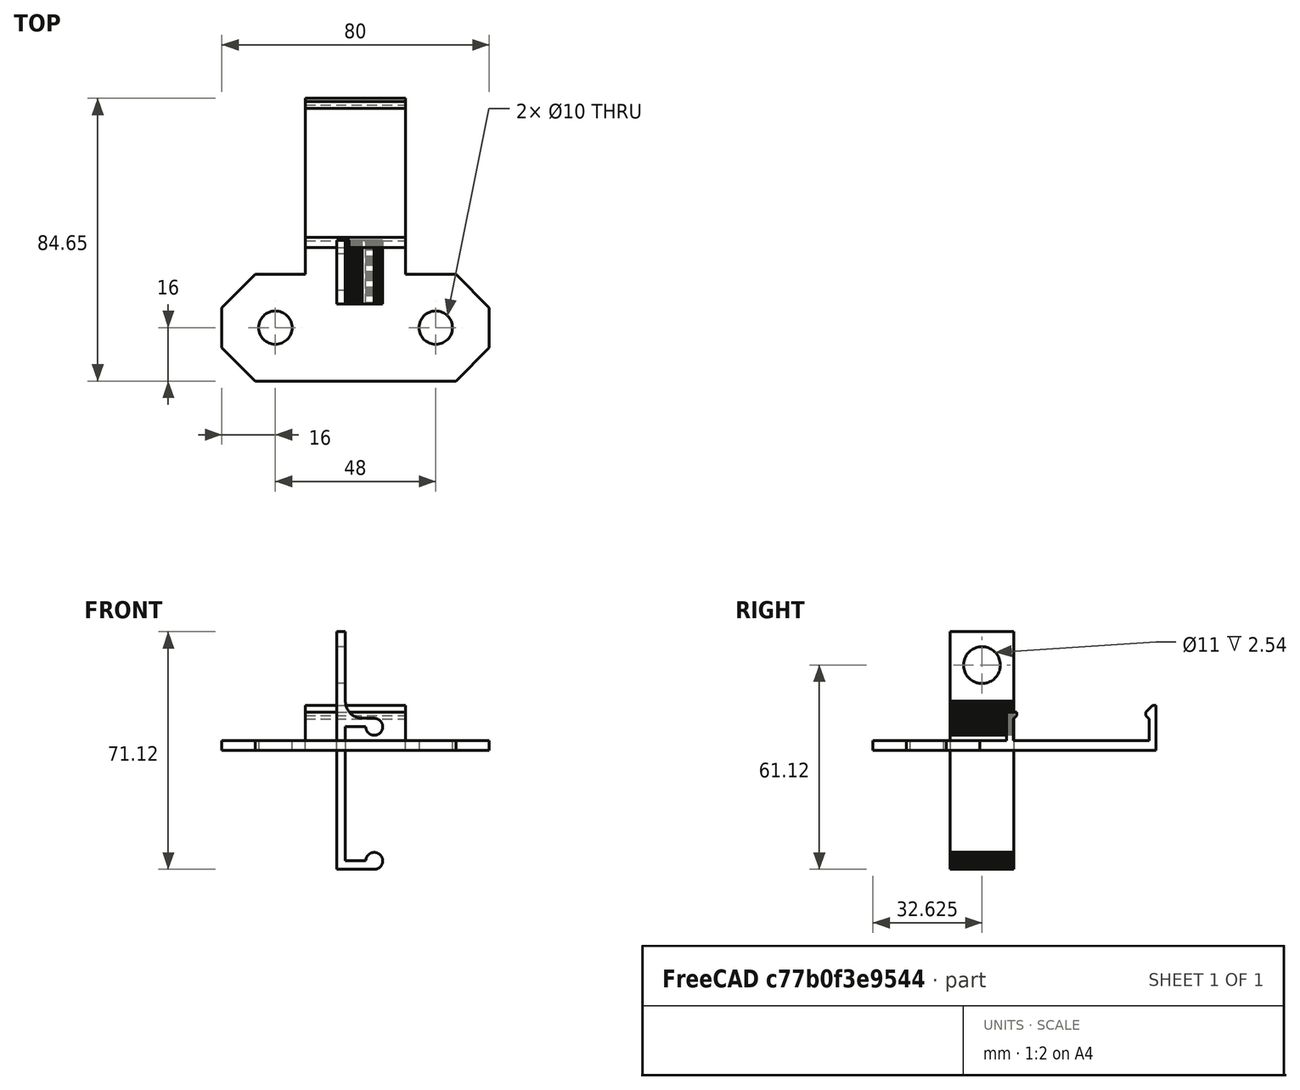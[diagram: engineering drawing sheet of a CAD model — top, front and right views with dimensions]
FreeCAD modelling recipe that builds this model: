
FCSTD DOCUMENT  (FreeCAD 0.20RUnknown)
Label: FilamentGuideRemix
License: All rights reserved
LicenseURL: http://en.wikipedia.org/wiki/All_rights_reserved
objects: Sketcher::SketchObject×7, PartDesign::Pocket×3, PartDesign::Pad×3, Part::Feature×2, PartDesign::Body×2, Mesh::Feature×1, PartDesign::FeatureBase×1, PartDesign::Plane×1, PartDesign::Hole×1, PartDesign::Chamfer×1
note: 29 computed .brp shape members not serialized (recipe doc carries the construction recipe); baked Part::Feature solids carry a one-line shape summary decoded from their .brp

FEATURE [Mesh::Feature] filament_guide2_clamp2  label="filament-guide2-clamp2"
FEATURE [Part::Feature] filament_guide2_clamp2001
  shape: bbox 21.34 x 19.05 x 71.12 mm, 2724 faces, 0 solids (baked)
FEATURE [Part::Feature] filament_guide2_clamp2001_solid  label="filament_guide2_clamp2001 (Solid)"
  shape: bbox 21.34 x 19.05 x 71.12 mm, 2724 faces (baked)
FEATURE [PartDesign::FeatureBase] BaseFeature
  BaseFeature = -> filament_guide2_clamp2001_solid
FEATURE [PartDesign::Plane] DatumPlane
  Length = 60
  MapMode = 5
  Placement = pos=(0,0,35.56) rot=(0,0,1;0rad)
  ResizeMode = 0
  Support = -> [BaseFeature]
  Width = 60
FEATURE [Sketcher::SketchObject] Sketch
  FullyConstrained = false
  MapMode = 5
  Placement = pos=(0,0,35.56) rot=(0,0,1;0rad)
  Support = -> [DatumPlane]
  sketch-geometry (4):
    g0: LineSegment StartX=-15.8199 StartY=4.12834 StartZ=0 EndX=12.2154 EndY=4.12834 EndZ=0
    g1: LineSegment StartX=12.2154 StartY=4.12834 StartZ=0 EndX=12.2154 EndY=-23.4291 EndZ=0
    g2: LineSegment StartX=12.2154 StartY=-23.4291 StartZ=0 EndX=-15.8199 EndY=-23.4291 EndZ=0
    g3: LineSegment StartX=-15.8199 StartY=-23.4291 StartZ=0 EndX=-15.8199 EndY=4.12834 EndZ=0
  constraints (8):
    c: Coincident(g0,g1)
    c: Coincident(g1,g2)
    c: Coincident(g2,g3)
    c: Coincident(g3,g0)
    c: Horizontal(g0)
    c: Horizontal(g2)
    c: Vertical(g1)
    c: Vertical(g3)
FEATURE [PartDesign::Pocket] Pocket
  BaseFeature = -> BaseFeature
  Direction = (0,0,-1)
  Length = 15
  Length2 = 5
  Profile = -> Sketch
  ReferenceAxis = -> Sketch [N_Axis]
  Type = 0
FEATURE [Sketcher::SketchObject] Sketch001
  ExternalGeometry = -> [Pocket]
  FullyConstrained = true
  MapMode = 5
  Placement = pos=(0,0,20.56) rot=(0,0,1;0rad)
  Support = -> [Pocket]
  sketch-geometry (4):
    g0: LineSegment StartX=-5.588 StartY=0 StartZ=0 EndX=-3.048 EndY=0 EndZ=0
    g1: LineSegment StartX=-3.048 StartY=0 StartZ=0 EndX=-3.048 EndY=-19.05 EndZ=0
    g2: LineSegment StartX=-3.048 StartY=-19.05 StartZ=0 EndX=-5.588 EndY=-19.05 EndZ=0
    g3: LineSegment StartX=-5.588 StartY=-19.05 StartZ=0 EndX=-5.588 EndY=0 EndZ=0
  constraints (10):
    c: Coincident(g0,g1)
    c: Coincident(g1,g2)
    c: Coincident(g2,g3)
    c: Coincident(g3,g0)
    c: Horizontal(g0)
    c: Horizontal(g2)
    c: Vertical(g1)
    c: Vertical(g3)
    c: Coincident(g0,g-3)
    c: Coincident(g1,g-6)
FEATURE [PartDesign::Pad] Pad
  BaseFeature = -> Pocket
  Direction = (0,0,1)
  Length = 15
  Length2 = 10
  Profile = -> Sketch001
  ReferenceAxis = -> Sketch001 [N_Axis]
  Type = 0
FEATURE [Sketcher::SketchObject] Sketch002
  ExternalGeometry = -> [Pad]
  FullyConstrained = true
  MapMode = 5
  Placement = pos=(-3.048,0,0) rot=(0.57735,0.57735,0.57735;2.0944rad)
  Support = -> [Pad]
  sketch-geometry (4):
    g0: Circle CenterX=-9.525 CenterY=25.56 CenterZ=0 NormalX=0 NormalY=0 NormalZ=1 AngleXU=0 Radius=2.5
    g1: LineSegment StartX=-19.05 StartY=35.56 StartZ=0 EndX=-9.525 EndY=35.56 EndZ=0
    g2: LineSegment StartX=0 StartY=35.56 StartZ=0 EndX=-9.525 EndY=35.56 EndZ=0
    g3: LineSegment StartX=-9.525 StartY=35.56 StartZ=0 EndX=-9.525 EndY=25.56 EndZ=0
  constraints (10):
    c: Diameter(g0) = 5
    c: Coincident(g1,g-5)
    c: PointOnObject(g1,g-3)
    c: Coincident(g2,g-3)
    c: Coincident(g2,g1)
    c: Equal(g1,g2)
    c: Coincident(g3,g1)
    c: Coincident(g3,g0)
    c: Vertical(g3)
    c: DistanceY(g3,g3) = 10
FEATURE [PartDesign::Hole] Hole
  BaseFeature = -> Pad
  CustomThreadClearance = 0
  Depth = 25
  DepthType = 0
  Diameter = 11
  DrillForDepth = false
  DrillPoint = 1
  DrillPointAngle = 118
  HoleCutCountersinkAngle = 90
  HoleCutCustomValues = false
  HoleCutDepth = 0
  HoleCutDiameter = 6.1
  HoleCutType = 0
  ModelThread = false
  Profile = -> Sketch002
  Tapered = false
  TaperedAngle = 90
  ThreadClass = 0
  ThreadDepth = 25
  ThreadDepthType = 0
  ThreadDirection = 0
  ThreadFit = 0
  ThreadSize = 18
  ThreadType = 1
  Threaded = false
  UseCustomThreadClearance = false
FEATURE [PartDesign::Body] Body
  BaseFeature = -> filament_guide2_clamp2001_solid
  Group = -> [BaseFeature,DatumPlane,Sketch,Pocket,Sketch001,Pad,Sketch002,Hole]
  Origin = -> Origin
  Tip = -> Hole
FEATURE [Sketcher::SketchObject] Sketch003
  FullyConstrained = true
  MapMode = 5
  Placement = pos=(0,0,0) rot=(0.57735,0.57735,0.57735;2.0944rad)
  Support = -> [YZ_Plane001]
  expr: Constraints[48] = 90 + 45
  expr: Constraints[49] = 90 + 45
  sketch-geometry (19):
    g0: LineSegment StartX=0 StartY=3.15 StartZ=0 EndX=40.35 EndY=3.15 EndZ=0
    g1: LineSegment StartX=40.35 StartY=3.15 StartZ=0 EndX=40.35 EndY=9.35 EndZ=0
    g2: LineSegment StartX=40.35 StartY=9.35 StartZ=0 EndX=0 EndY=9.35 EndZ=0
    g3: LineSegment StartX=0 StartY=9.35 StartZ=0 EndX=0 EndY=3.15 EndZ=0
    g4: LineSegment StartX=42.5 StartY=0 StartZ=0 EndX=42.5 EndY=11.5 EndZ=0
    g5: LineSegment StartX=42.5 StartY=11.5 StartZ=0 EndX=39.5 EndY=11.5 EndZ=0
    g6: LineSegment StartX=39.5 StartY=11.5 StartZ=0 EndX=39.5 EndY=10.5 EndZ=0
    g7: LineSegment StartX=39.5 StartY=10.5 StartZ=0 EndX=40.5 EndY=9.5 EndZ=0
    g8: LineSegment StartX=40.5 StartY=9.5 StartZ=0 EndX=40.5 EndY=3 EndZ=0
    g9: LineSegment StartX=40.5 StartY=3 StartZ=0 EndX=-0.15 EndY=3 EndZ=0
    g10: LineSegment StartX=-0.15 StartY=3 StartZ=0 EndX=-0.15 EndY=9.5 EndZ=0
    g11: LineSegment StartX=-0.15 StartY=9.5 StartZ=0 EndX=0.85 EndY=10.5 EndZ=0
    g12: LineSegment StartX=0.85 StartY=10.5 StartZ=0 EndX=0.85 EndY=11.5 EndZ=0
    g13: LineSegment StartX=0.85 StartY=11.5 StartZ=0 EndX=-2.15 EndY=11.5 EndZ=0
    g14: LineSegment StartX=-2.15 StartY=11.5 StartZ=0 EndX=-2.15 EndY=3 EndZ=0
    g15: LineSegment StartX=-2.15 StartY=3 StartZ=0 EndX=-42.15 EndY=3 EndZ=0
    g16: LineSegment StartX=-42.15 StartY=3 StartZ=0 EndX=-42.15 EndY=0 EndZ=0
    g17: LineSegment StartX=-42.15 StartY=0 StartZ=0 EndX=42.5 EndY=0 EndZ=0
    g18: LineSegment StartX=-2.15 StartY=3 StartZ=0 EndX=-0.15 EndY=3 EndZ=0
  constraints (56):
    c: Coincident(g0,g1)
    c: Coincident(g1,g2)
    c: Coincident(g2,g3)
    c: Coincident(g3,g0)
    c: Horizontal(g0)
    c: Horizontal(g2)
    c: Vertical(g1)
    c: Vertical(g3)
    c: DistanceX(g2,g2) = 40.35
    c: DistanceY(g1,g1) = 6.2
    c: PointOnObject(g0,g-2)
    c: PointOnObject(g4,g-1)
    c: Vertical(g4)
    c: Coincident(g4,g5)
    c: Horizontal(g5)
    c: Coincident(g5,g6)
    c: Vertical(g6)
    c: Coincident(g6,g7)
    c: Coincident(g7,g8)
    c: Coincident(g8,g9)
    c: Horizontal(g9)
    c: Coincident(g9,g10)
    c: Vertical(g10)
    c: Coincident(g10,g11)
    c: Coincident(g11,g12)
    c: Vertical(g12)
    c: Coincident(g12,g13)
    c: Horizontal(g13)
    c: Coincident(g13,g14)
    c: Vertical(g14)
    c: Coincident(g14,g15)
    c: Horizontal(g15)
    c: Coincident(g15,g16)
    c: PointOnObject(g16,g-1)
    c: Vertical(g16)
    c: Coincident(g16,g17)
    c: Coincident(g17,g4)
    c: Vertical(g8)
    c: Coincident(g18,g14)
    c: Coincident(g18,g9)
    c: Horizontal(g18)
    c: DistanceY(g9,g0) = 0.15
    c: DistanceX(g0,g8) = 0.15
    c: DistanceX(g9,g0) = 0.15
    c: DistanceY(g2,g10) = 0.15
    c: Equal(g8,g10)
    c: Equal(g12,g6)
    c: Equal(g11,g7)
    c: Angle(g12,g11) = 2.35619
    c: Angle(g7,g6) = 2.35619
    c: DistanceX(g10,g11) = 1
    c: DistanceX(g5,g5) = 3
    c: DistanceY(g6,g6) = 1
    c: DistanceY(g4,g8) = 3
    c: Equal(g13,g5)
    c: DistanceX(g15,g15) = 40
FEATURE [PartDesign::Pad] Pad001
  Direction = (1,-2e-16,3e-16)
  Length = 80
  Length2 = 10
  Midplane = true
  Placement = pos=(0,0,0) rot=(0.57735,0.57735,0.57735;2.0944rad)
  Profile = -> Sketch003
  ReferenceAxis = -> Sketch003 [N_Axis]
  Type = 0
FEATURE [Sketcher::SketchObject] Sketch004
  ExternalGeometry = -> [Pad001]
  FullyConstrained = true
  MapMode = 5
  Support = -> [XY_Plane001]
  sketch-geometry (10):
    g0: LineSegment StartX=-45 StartY=-10.15 StartZ=0 EndX=-15 EndY=-10.15 EndZ=0
    g1: LineSegment StartX=-15 StartY=-10.15 StartZ=0 EndX=-15 EndY=47.5 EndZ=0
    g2: LineSegment StartX=-15 StartY=47.5 StartZ=0 EndX=-45 EndY=47.5 EndZ=0
    g3: LineSegment StartX=-45 StartY=47.5 StartZ=0 EndX=-45 EndY=-10.15 EndZ=0
    g4: LineSegment StartX=15 StartY=47.5 StartZ=0 EndX=45 EndY=47.5 EndZ=0
    g5: LineSegment StartX=45 StartY=47.5 StartZ=0 EndX=45 EndY=-10.15 EndZ=0
    g6: LineSegment StartX=45 StartY=-10.15 StartZ=0 EndX=15 EndY=-10.15 EndZ=0
    g7: LineSegment StartX=15 StartY=-10.15 StartZ=0 EndX=15 EndY=47.5 EndZ=0
    g8: LineSegment StartX=-15 StartY=47.5 StartZ=0 EndX=0 EndY=47.5 EndZ=0
    g9: LineSegment StartX=0 StartY=47.5 StartZ=0 EndX=15 EndY=47.5 EndZ=0
  constraints (29):
    c: Coincident(g0,g1)
    c: Coincident(g1,g2)
    c: Coincident(g2,g3)
    c: Coincident(g3,g0)
    c: Horizontal(g0)
    c: Horizontal(g2)
    c: Vertical(g1)
    c: Vertical(g3)
    c: Coincident(g4,g5)
    c: Coincident(g5,g6)
    c: Coincident(g6,g7)
    c: Coincident(g7,g4)
    c: Horizontal(g4)
    c: Horizontal(g6)
    c: Vertical(g5)
    c: Vertical(g7)
    c: Equal(g2,g4)
    c: Equal(g5,g3)
    c: Coincident(g1,g8)
    c: PointOnObject(g8,g-2)
    c: Horizontal(g8)
    c: Coincident(g8,g9)
    c: Coincident(g9,g4)
    c: Horizontal(g9)
    c: Equal(g8,g9)
    c: DistanceY(g0,g-3) = 8
    c: DistanceX(g0,g-3) = 5
    c: DistanceY(g-4,g2) = 5
    c: DistanceX(g1,g4) = 30
FEATURE [PartDesign::Pocket] Pocket001
  BaseFeature = -> Pad001
  Direction = (0,0,-1)
  Length = 5
  Length2 = 5
  Placement = pos=(0,0,0) rot=(0.57735,0.57735,0.57735;2.0944rad)
  Profile = -> Sketch004
  ReferenceAxis = -> Sketch004 [N_Axis]
  Reversed = true
  Type = 1
FEATURE [Sketcher::SketchObject] Sketch005
  ExternalGeometry = -> [Pocket001]
  FullyConstrained = true
  MapMode = 5
  Support = -> [XY_Plane001]
  sketch-geometry (7):
    g0: Circle CenterX=-24 CenterY=-26.15 CenterZ=0 NormalX=0 NormalY=0 NormalZ=1 AngleXU=0 Radius=5
    g1: Circle CenterX=24 CenterY=-26.15 CenterZ=0 NormalX=0 NormalY=0 NormalZ=1 AngleXU=0 Radius=5
    g2: LineSegment StartX=-24 StartY=-26.15 StartZ=0 EndX=0 EndY=-26.15 EndZ=0
    g3: LineSegment StartX=0 StartY=-26.15 StartZ=0 EndX=24 EndY=-26.15 EndZ=0
    g4: LineSegment StartX=-24 StartY=-26.15 StartZ=0 EndX=-24 EndY=-10.15 EndZ=0
    g5: LineSegment StartX=-24 StartY=-26.15 StartZ=0 EndX=-40 EndY=-26.15 EndZ=0
    g6: LineSegment StartX=-24 StartY=-26.15 StartZ=0 EndX=-24 EndY=-42.15 EndZ=0
  constraints (20):
    c: Coincident(g2,g0)
    c: PointOnObject(g2,g-2)
    c: Horizontal(g2)
    c: Coincident(g2,g3)
    c: Coincident(g3,g1)
    c: Equal(g2,g3)
    c: Equal(g0,g1)
    c: Horizontal(g3)
    c: Coincident(g4,g0)
    c: PointOnObject(g4,g-5)
    c: Vertical(g4)
    c: Coincident(g5,g0)
    c: PointOnObject(g5,g-3)
    c: Horizontal(g5)
    c: Coincident(g6,g0)
    c: PointOnObject(g6,g-6)
    c: Vertical(g6)
    c: Equal(g4,g5)
    c: Equal(g6,g5)
    c: Diameter(g0) = 10
FEATURE [PartDesign::Pocket] Pocket002
  BaseFeature = -> Pocket001
  Direction = (0,0,-1)
  Length = 5
  Length2 = 5
  Placement = pos=(0,0,0) rot=(0.57735,0.57735,0.57735;2.0944rad)
  Profile = -> Sketch005
  ReferenceAxis = -> Sketch005 [N_Axis]
  Reversed = true
  Type = 1
FEATURE [PartDesign::Chamfer] Chamfer
  Angle = 45
  Base = -> Pocket002 [Edge58,Edge56,Edge55,Edge57]
  BaseFeature = -> Pocket002
  ChamferType = 0
  FlipDirection = false
  Placement = pos=(0,0,0) rot=(0.57735,0.57735,0.57735;2.0944rad)
  Size = 10
  Size2 = 1
  SupportTransform = false
  UseAllEdges = false
FEATURE [Sketcher::SketchObject] Sketch006
  ExternalGeometry = -> [Chamfer]
  FullyConstrained = true
  MapMode = 5
  Placement = pos=(-15,0,-3.3e-15) rot=(0.57735,0.57735,-0.57735;4.18879rad)
  Support = -> [Chamfer]
  sketch-geometry (6):
    g0: LineSegment StartX=39.5 StartY=-11.5 StartZ=0 EndX=41.5 EndY=-13.5 EndZ=0
    g1: LineSegment StartX=41.5 StartY=-13.5 StartZ=0 EndX=42.5 EndY=-13.5 EndZ=0
    g2: LineSegment StartX=42.5 StartY=-13.5 StartZ=0 EndX=42.5 EndY=-11.5 EndZ=0
    g3: LineSegment StartX=39.5 StartY=-11.5 StartZ=0 EndX=39.5 EndY=-10.5 EndZ=0
    g4: LineSegment StartX=39.5 StartY=-10.5 StartZ=0 EndX=42.5 EndY=-10.5 EndZ=0
    g5: LineSegment StartX=42.5 StartY=-10.5 StartZ=0 EndX=42.5 EndY=-11.5 EndZ=0
  constraints (15):
    c: Coincident(g0,g1)
    c: Horizontal(g1)
    c: Coincident(g1,g2)
    c: Vertical(g2)
    c: DistanceX(g1,g1) = 1
    c: Coincident(g-3,g0)
    c: Coincident(g-3,g2)
    c: Coincident(g0,g3)
    c: Coincident(g3,g4)
    c: Horizontal(g4)
    c: Coincident(g4,g5)
    c: Coincident(g5,g2)
    c: Vertical(g5)
    c: Angle(g0,g3) = 2.35619
    c: Coincident(g3,g-4)
FEATURE [PartDesign::Pad] Pad002
  BaseFeature = -> Chamfer
  Direction = (-1,-1e-16,-1e-16)
  Length = 30
  Length2 = 10
  Placement = pos=(0,0,0) rot=(0.57735,0.57735,0.57735;2.0944rad)
  Profile = -> Sketch006
  ReferenceAxis = -> Sketch006 [N_Axis]
  Reversed = true
  Type = 0
FEATURE [PartDesign::Body] Body001  label="BodyOwn"
  Group = -> [Sketch003,Pad001,Sketch004,Pocket001,Sketch005,Pocket002,Chamfer,Sketch006,Pad002]
  Origin = -> Origin001
  Tip = -> Pad002
